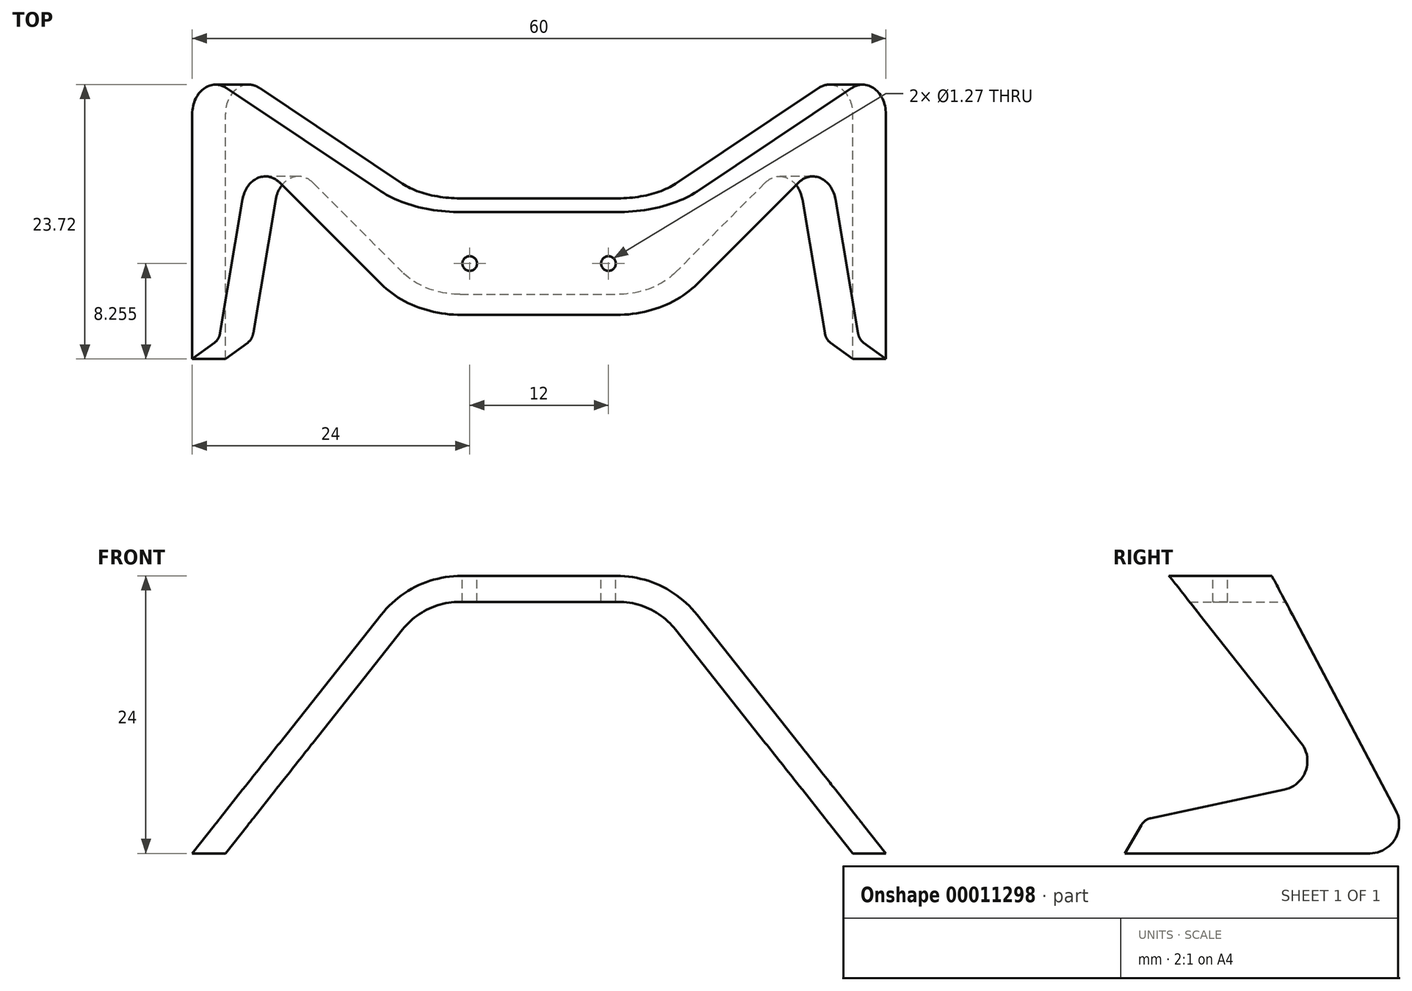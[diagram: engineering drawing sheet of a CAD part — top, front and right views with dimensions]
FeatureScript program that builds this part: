
annotation { "Feature Type Name" : "Feature", "Feature Type Description" : "" }
export const myFeature = defineFeature(function(context is Context, id is Id, definition is map)
    precondition{}
    {
        {
            var Q0;
            Q0=qCreatedBy(makeId("Front.planeOp"),FACE);
            var sketch = newSketch(context, id + "F0", { "sketchPlane" : qUnion([Q0])});
            skLineSegment(sketch, "E0", {"start": v(-27.13, 0) * mm, "end": v(-11.82, 19.34) * mm});
            skLineSegment(sketch, "E1", {"start": v(-6.84, 21.75) * mm, "end": v(0, 21.75) * mm});
            skLineSegment(sketch, "E2", {"start": v(0, 24) * mm, "end": v(-6.7, 24) * mm});
            skLineSegment(sketch, "E3", {"start": v(-13.67, 20.63) * mm, "end": v(-30, 0) * mm});
            skLineSegment(sketch, "E4", {"start": v(-30, 0) * mm, "end": v(-27.13, 0) * mm});
            skLineSegment(sketch, "E5", {"start": v(0, 24) * mm, "end": v(0, 0) * mm, "construction": true});
            skPoint(sketch, "E6.visualSharp", {"position": v(-9.91, 21.75) * mm});
            skArc(sketch, "E6.filletArc", {"start": v(-6.84, 21.75) * mm, "mid": v(-9.6, 21.12) * mm, "end": v(-11.82, 19.34) * mm});
            skPoint(sketch, "E7.visualSharp", {"position": v(-11, 24) * mm});
            skArc(sketch, "E7.filletArc", {"start": v(-6.7, 24) * mm, "mid": v(-10.57, 23.11) * mm, "end": v(-13.67, 20.63) * mm});
            skLineSegment(sketch, "E8.0.MirrorCS", {"start": v(0, 24) * mm, "end": v(6.7, 24) * mm});
            skLineSegment(sketch, "E9.0.MirrorCS", {"start": v(6.84, 21.75) * mm, "end": v(0, 21.75) * mm});
            skArc(sketch, "E10.0.MirrorCS", {"start": v(6.84, 21.75) * mm, "mid": v(9.6, 21.12) * mm, "end": v(11.82, 19.34) * mm});
            skArc(sketch, "E11.0.MirrorCS", {"start": v(6.7, 24) * mm, "mid": v(10.57, 23.11) * mm, "end": v(13.67, 20.63) * mm});
            skLineSegment(sketch, "E12.0.MirrorCS", {"start": v(13.67, 20.63) * mm, "end": v(30, 0) * mm});
            skLineSegment(sketch, "E13.0.MirrorCS", {"start": v(27.13, 0) * mm, "end": v(11.82, 19.34) * mm});
            skLineSegment(sketch, "E14.0.MirrorCS", {"start": v(30, 0) * mm, "end": v(27.13, 0) * mm});
            skSolve(sketch);
        }
        {
            var Q0;
            Q0=makeQuery(id+"F0.imprint","IMPRINT",FACE,{"disambiguationData":[TD([[makeQuery(id+"F0.imprint","IMPRINT",EDGE,{"derivedFrom":sQuery(id+"F0.wireOp",EDGE,"E0")}),1.0]])]});
            extrude(context, id + "F1", {"entities" : qUnion([Q0]), "depth" : 50.8 * mm});
        }
        {
            var Q0;
            Q0=qCreatedBy(makeId("Right.planeOp"),FACE);
            var sketch = newSketch(context, id + "F2", { "sketchPlane" : qUnion([Q0])});
            skLineSegment(sketch, "E15", {"start": v(0, 0) * mm, "end": v(-12.7, 24) * mm});
            skLineSegment(sketch, "E16", {"start": v(-12.7, 24) * mm, "end": v(0, 24) * mm});
            skLineSegment(sketch, "E17", {"start": v(0, 24) * mm, "end": v(0, 0) * mm});
            skSolve(sketch);
        }
        {
            var Q0;
            Q0 = qSketchRegion(id + "F2", true);
            extrude(context, id + "F3", {"entities" : qUnion([Q0]), "operationType" : NewBodyOperationType.REMOVE, "depth" : 76.2 * mm, "hasSecondDirection" : true, "secondDirectionOppositeDirection" : true, "secondDirectionDepth" : 76.2 * mm});
        }
        {
            var Q0;
            Q0=qCreatedBy(makeId("Right.planeOp"),FACE);
            var sketch = newSketch(context, id + "F4", { "sketchPlane" : qUnion([Q0])});
            skLineSegment(sketch, "E18", {"start": v(-21.6, 24) * mm, "end": v(-7.62, 6.35) * mm});
            skLineSegment(sketch, "E19", {"start": v(-7.62, 6.35) * mm, "end": v(-23.7, 2.93) * mm});
            skLineSegment(sketch, "E20", {"start": v(-23.7, 2.93) * mm, "end": v(-25.4, 0) * mm});
            skLineSegment(sketch, "E21", {"start": v(-25.4, 0) * mm, "end": v(-52.77, 0) * mm});
            skLineSegment(sketch, "E22", {"start": v(-52.77, 0) * mm, "end": v(-52.77, 24) * mm});
            skLineSegment(sketch, "E23", {"start": v(-52.77, 24) * mm, "end": v(-21.59, 24) * mm});
            skSolve(sketch);
        }
        {
            var Q0;
            Q0 = qSketchRegion(id + "F4", true);
            extrude(context, id + "F5", {"entities" : qUnion([Q0]), "operationType" : NewBodyOperationType.REMOVE, "endBound" : BoundingType.THROUGH_ALL, "oppositeDirection" : true, "depth" : 25.4 * mm, "hasSecondDirection" : true, "secondDirectionBound" : SecondDirectionBoundingType.THROUGH_ALL, "secondDirectionOppositeDirection" : false, "secondDirectionDepth" : 25.4 * mm});
        }
        {
            var Q0;
            Q0=makeQuery(id+"F3.boolean.opBoolean","MERGE",EDGE,{"derivedFrom":[makeQuery(id+"F1.opExtrude","CAP_EDGE",EDGE,{"disambiguationData":[OSD([sQuery(id+"F0.wireOp",EDGE,"E14.0.MirrorCS")])],"isStart":true}),makeQuery(id+"F3.opExtrude","SWEPT_EDGE",EDGE,{"disambiguationData":[OSD([sQuery(id+"F2.wireOp",EDGE,"E15"),sQuery(id+"F2.wireOp",EDGE,"E17")])]})]});
            var Q1;
            Q1=makeQuery(id+"F3.boolean.opBoolean","MERGE",EDGE,{"derivedFrom":[makeQuery(id+"F1.opExtrude","CAP_EDGE",EDGE,{"disambiguationData":[OSD([sQuery(id+"F0.wireOp",EDGE,"E4")])],"isStart":true}),makeQuery(id+"F3.opExtrude","SWEPT_EDGE",EDGE,{"disambiguationData":[OSD([sQuery(id+"F2.wireOp",EDGE,"E15"),sQuery(id+"F2.wireOp",EDGE,"E17")])]})]});
            fillet(context, id + "F6", {"entities" : qUnion([Q0, Q1]), "radius" : 2.54 * mm, "tangentPropagation" : true, "allowEdgeOverflow" : false});
        }
        {
            var Q0;
            Q0=makeQuery(id+"F5.boolean.opBoolean","COPY",EDGE,{"disambiguationData":[OD(0.0)],"derivedFrom":makeQuery(id+"F5.opExtrude","SWEPT_EDGE",EDGE,{"disambiguationData":[OSD([sQuery(id+"F4.wireOp",EDGE,"E18"),sQuery(id+"F4.wireOp",EDGE,"E19")])]})});
            var Q1;
            Q1=makeQuery(id+"F5.boolean.opBoolean","COPY",EDGE,{"disambiguationData":[OD(1.0)],"derivedFrom":makeQuery(id+"F5.opExtrude","SWEPT_EDGE",EDGE,{"disambiguationData":[OSD([sQuery(id+"F4.wireOp",EDGE,"E18"),sQuery(id+"F4.wireOp",EDGE,"E19")])]})});
            fillet(context, id + "F7", {"entities" : qUnion([Q0, Q1]), "radius" : 2.54 * mm, "tangentPropagation" : true, "allowEdgeOverflow" : false});
        }
        {
            var Q0;
            Q0=makeQuery(id+"F5.boolean.opBoolean","COPY",EDGE,{"disambiguationData":[OD(1.0)],"derivedFrom":makeQuery(id+"F5.opExtrude","SWEPT_EDGE",EDGE,{"disambiguationData":[OSD([sQuery(id+"F4.wireOp",EDGE,"E19"),sQuery(id+"F4.wireOp",EDGE,"E20")])]})});
            var Q1;
            Q1=makeQuery(id+"F5.boolean.opBoolean","COPY",EDGE,{"disambiguationData":[OD(0.0)],"derivedFrom":makeQuery(id+"F5.opExtrude","SWEPT_EDGE",EDGE,{"disambiguationData":[OSD([sQuery(id+"F4.wireOp",EDGE,"E19"),sQuery(id+"F4.wireOp",EDGE,"E20")])]})});
            fillet(context, id + "F8", {"entities" : qUnion([Q0, Q1]), "radius" : 1.27 * mm, "tangentPropagation" : true, "allowEdgeOverflow" : false});
        }
        {
            var Q0;
            Q0=makeQuery(id+"F1.opExtrude","SWEPT_FACE",FACE,{"disambiguationData":[OSD([sQuery(id+"F0.wireOp",EDGE,"E2"),sQuery(id+"F0.wireOp",EDGE,"E8.0.MirrorCS")])]});
            var sketch = newSketch(context, id + "F9", { "sketchPlane" : qUnion([Q0])});
            skLineSegment(sketch, "E24", {"start": v(6.7, -17.15) * mm, "end": v(-6.7, -17.15) * mm, "construction": true});
            skCircle(sketch, "E25", {"center": v(0, -17.15) * mm, "radius": 6 * mm, "construction": true});
            skCircle(sketch, "E26", {"center": v(6, -17.15) * mm, "radius": 0.64 * mm});
            skCircle(sketch, "E27", {"center": v(-6, -17.15) * mm, "radius": 0.64 * mm});
            skSolve(sketch);
        }
        {
            var Q0;
            Q0 = qSketchRegion(id + "F9", true);
            extrude(context, id + "F10", {"entities" : qUnion([Q0]), "operationType" : NewBodyOperationType.REMOVE, "oppositeDirection" : true, "depth" : 25.4 * mm});
        }
    });
